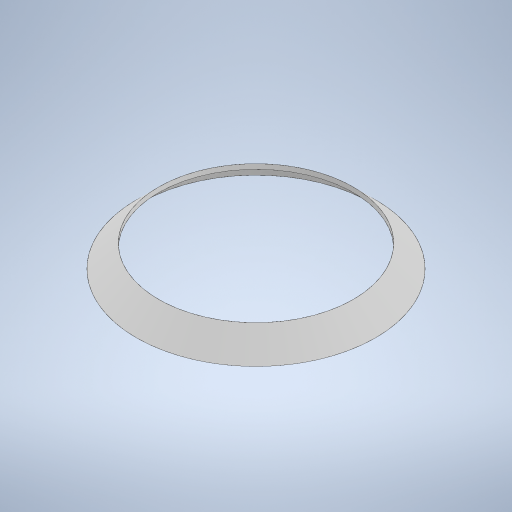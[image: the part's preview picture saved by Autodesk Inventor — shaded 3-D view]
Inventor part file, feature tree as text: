
AUTODESK INVENTOR PART (.ipt)
format: ipt  version: 2024.3 (Build 283343000, 343)  size: 244,224 bytes
history: native  units: mm
features: revolve x1, sketch x1
ambient origin geometry x8: Origin, YZ Plane, XZ Plane, XY Plane, X Axis, Y Axis, Z Axis, Center Point
bodies: Solid1 (feature_tree)
feature tree (2):
  revolve  "Revolution1"  [1 undecoded]
  sketch  "Sketch1"  dims[d0=57.0mm d1=13.0mm d2=2.0mm d3=13.0mm d4=135.0deg d5=90.0deg]
note: 1 required parameter value undecoded (feature->parameter linkage not recoverable at this tier; creation-order binding heuristic only, values carry confidence <= 0.55)
